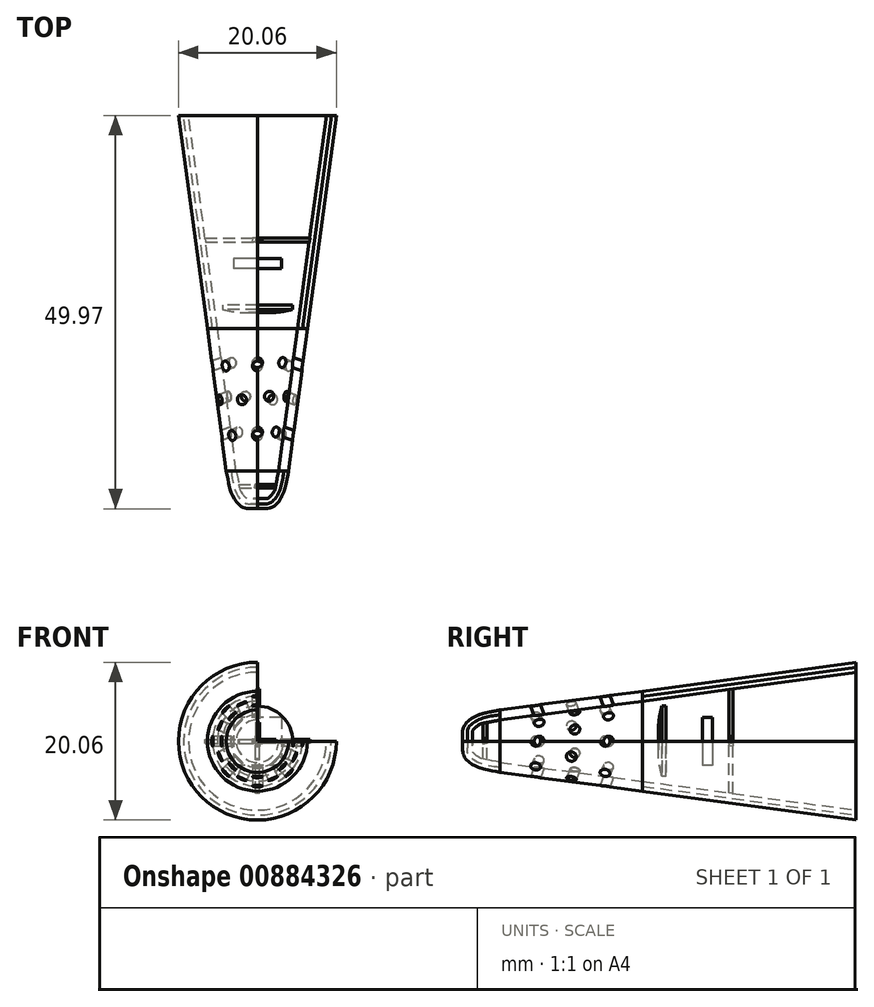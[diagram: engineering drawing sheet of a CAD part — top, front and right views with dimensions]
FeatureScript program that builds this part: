
annotation { "Feature Type Name" : "Feature", "Feature Type Description" : "" }
export const myFeature = defineFeature(function(context is Context, id is Id, definition is map)
    precondition{}
    {
        {
            var Q0;
            Q0=qCreatedBy(makeId("Right.planeOp"),FACE);
            var sketch = newSketch(context, id + "F0", { "sketchPlane" : qUnion([Q0])});
            skFitSpline(sketch, "E0", {"points": [v(0, 0) * mm, v(0, 1.1) * mm, v(0.45, 2.3) * mm, v(2.09, 3.34) * mm, v(4.76, 3.97) * mm], "startDerivative": vector(-0.16, 5.28) * mm, "endDerivative": vector(14.36, 3.06) * mm});
            skLineSegment(sketch, "E1", {"start": v(4.76, 3.97) * mm, "end": v(22.86, 6.35) * mm});
            skLineSegment(sketch, "E2", {"start": v(22.86, 6.35) * mm, "end": v(22.86, 0) * mm});
            skLineSegment(sketch, "E3", {"start": v(22.86, 0) * mm, "end": v(0, 0) * mm});
            skLineSegment(sketch, "E4", {"start": v(0, 0) * mm, "end": v(44.4, 0) * mm, "construction": true});
            skFitSpline(sketch, "E5", {"points": [v(1.27, 0) * mm, v(1.27, 1.1) * mm, v(1.34, 1.4) * mm, v(2.09, 2.07) * mm, v(4.76, 2.69) * mm], "startDerivative": vector(-0.16, 5.28) * mm, "endDerivative": vector(14.36, 3.06) * mm});
            skLineSegment(sketch, "E6", {"start": v(4.76, 2.69) * mm, "end": v(22.86, 5.08) * mm});
            skLineSegment(sketch, "E7", {"start": v(4.76, 3.97) * mm, "end": v(4.76, 2.69) * mm});
            skFitSpline(sketch, "E8", {"points": [v(0.62, 0) * mm, v(0.6, 1.05) * mm, v(0.7, 1.6) * mm, v(1.34, 2.32) * mm, v(2.5, 2.9) * mm, v(3.81, 3.22) * mm, v(4.76, 3.33) * mm], "startDerivative": vector(-0.15, 6.7) * mm, "endDerivative": vector(5.58, 0.48) * mm});
            skLineSegment(sketch, "E9", {"start": v(0.62, 0) * mm, "end": v(1.27, 0) * mm});
            skLineSegment(sketch, "E10", {"start": v(4.76, 3.33) * mm, "end": v(4.76, 2.69) * mm});
            skSolve(sketch);
        }
        {
            var Q0;
            {var subQ0=sQuery(id+"F0.wireOp",EDGE,"E0");Q0=makeQuery(id+"F0.imprint","IMPRINT",FACE,{"disambiguationData":[TD([[makeQuery(id+"F0.imprint","IMPRINT",EDGE,{"derivedFrom":subQ0}),-1.0]])]});}
            var Q1;
            Q1=sQuery(id+"F0.wireOp",EDGE,"E4");
            revolve(context, id + "F1", {"surfaceOperationType" : NewSurfaceOperationType.NEW, "entities" : qUnion([Q0]), "axis" : qUnion([Q1]), "revolveType" : RevolveType.FULL});
        }
        {
            var Q0;
            Q0=qCreatedBy(makeId("Right.planeOp"),FACE);
            var sketch = newSketch(context, id + "F2", { "sketchPlane" : qUnion([Q0])});
            skLineSegment(sketch, "E11", {"start": v(0, 0) * mm, "end": v(22.86, 0) * mm});
            skLineSegment(sketch, "E12", {"start": v(22.86, 0) * mm, "end": v(22.86, 6.35) * mm});
            skLineSegment(sketch, "E13", {"start": v(22.86, 6.35) * mm, "end": v(49.95, 10.03) * mm});
            skLineSegment(sketch, "E14", {"start": v(49.95, 10.03) * mm, "end": v(49.95, 0) * mm});
            skLineSegment(sketch, "E15", {"start": v(49.95, 0) * mm, "end": v(22.86, 0) * mm});
            skLineSegment(sketch, "E16", {"start": v(22.86, 6.35) * mm, "end": v(22.86, 5.08) * mm});
            skLineSegment(sketch, "E17", {"start": v(22.86, 5.08) * mm, "end": v(49.95, 8.76) * mm});
            skLineSegment(sketch, "E18", {"start": v(49.95, 8.76) * mm, "end": v(49.95, 10.03) * mm});
            skLineSegment(sketch, "E19", {"start": v(22.86, 5.71) * mm, "end": v(49.95, 9.4) * mm});
            skSolve(sketch);
        }
        {
            var Q0;
            {var subQ2=sQuery(id+"F2.wireOp",EDGE,"E13");Q0=makeQuery(id+"F2.imprint","IMPRINT",FACE,{"disambiguationData":[TD([[makeQuery(id+"F2.imprint","IMPRINT",EDGE,{"derivedFrom":subQ2}),-1.0]])]});}
            var Q1;
            Q1=sQuery(id+"F2.wireOp",EDGE,"E15");
            revolve(context, id + "F3", {"operationType" : NewBodyOperationType.ADD, "surfaceOperationType" : NewSurfaceOperationType.NEW, "entities" : qUnion([Q0]), "axis" : qUnion([Q1]), "revolveType" : RevolveType.FULL});
        }
        {
            var Q0;
            {var subQ4=sQuery(id+"F0.wireOp",EDGE,"E1");Q0=makeQuery(id+"F0.imprint","IMPRINT",FACE,{"disambiguationData":[TD([[makeQuery(id+"F0.imprint","IMPRINT",EDGE,{"derivedFrom":subQ4}),-1.0]])]});}
            var Q1;
            Q1=sQuery(id+"F0.wireOp",EDGE,"E3");
            revolve(context, id + "F4", {"surfaceOperationType" : NewSurfaceOperationType.NEW, "entities" : qUnion([Q0]), "axis" : qUnion([Q1]), "revolveType" : RevolveType.FULL});
        }
        {
            var Q0;
            {var subQ2=sQuery(id+"F2.wireOp",EDGE,"E17");Q0=makeQuery(id+"F2.imprint","IMPRINT",FACE,{"disambiguationData":[TD([[makeQuery(id+"F2.imprint","IMPRINT",EDGE,{"derivedFrom":subQ2}),1.0]])]});}
            var Q1;
            Q1=sQuery(id+"F2.wireOp",EDGE,"E15");
            revolve(context, id + "F5", {"surfaceOperationType" : NewSurfaceOperationType.NEW, "entities" : qUnion([Q0]), "axis" : qUnion([Q1]), "revolveType" : RevolveType.FULL});
        }
        {
            var Q0;
            {var subQ0=sQuery(id+"F0.wireOp",EDGE,"E5");Q0=makeQuery(id+"F0.imprint","IMPRINT",FACE,{"disambiguationData":[TD([[makeQuery(id+"F0.imprint","IMPRINT",EDGE,{"derivedFrom":subQ0}),1.0]])]});}
            var Q1;
            Q1=sQuery(id+"F2.wireOp",EDGE,"E11");
            revolve(context, id + "F6", {"surfaceOperationType" : NewSurfaceOperationType.NEW, "entities" : qUnion([Q0]), "axis" : qUnion([Q1]), "revolveType" : RevolveType.FULL});
        }
        {
            var Q0;
            Q0=sQuery(id+"F0.wireOp",EDGE,"E1");
            cPlane(context, id + "F7", {"entities" : qUnion([Q0]), "cplaneType" : CPlaneType.LINE_ANGLE, "offset" : 25.4 * mm, "angle" : 0 * degree, "width" : 152.4 * mm, "height" : 152.4 * mm});
        }
        {
            var Q0;
            Q0=qCreatedBy(id+"F7.planeOp",FACE);
            var sketch = newSketch(context, id + "F8", { "sketchPlane" : qUnion([Q0])});
            skCircle(sketch, "E20", {"center": v(0, 9.8) * mm, "radius": 0.64 * mm});
            skCircle(sketch, "E21", {"center": v(0, 18.7) * mm, "radius": 0.64 * mm});
            skLineSegment(sketch, "E22", {"start": v(0, 5.23) * mm, "end": v(0, 23.5) * mm});
            skSolve(sketch);
        }
        {
            var Q0;
            Q0=qCreatedBy(makeId("Right.planeOp"),FACE);
            var sketch = newSketch(context, id + "F9", { "sketchPlane" : qUnion([Q0])});
            skLineSegment(sketch, "E23", {"start": v(9.29, 4.57) * mm, "end": v(9.81, 3.13) * mm});
            skLineSegment(sketch, "E24", {"start": v(9.29, 4.57) * mm, "end": v(9.29, 0) * mm, "construction": true});
            skLineSegment(sketch, "E25", {"start": v(18.1, 5.72) * mm, "end": v(18.62, 4.3) * mm});
            skLineSegment(sketch, "E26", {"start": v(18.1, 5.72) * mm, "end": v(18.1, 0) * mm, "construction": true});
            skSolve(sketch);
        }
        {
            var Q0;
            {var subQ0=sQuery(id+"F8.wireOp",EDGE,"E22");var subQ1=sQuery(id+"F8.wireOp",EDGE,"E20");var subQ2=makeQuery(id+"F8.imprint","INTERSECT",VERTEX,{"disambiguationData":[OD(0.0)],"derivedFrom":[subQ1,subQ0]});Q0=makeQuery(id+"F8.imprint","IMPRINT",FACE,{"disambiguationData":[TD([[makeQuery(id+"F8.imprint","IMPRINT",EDGE,{"disambiguationData":[TD([[subQ2,1.0]])],"derivedFrom":subQ1}),1.0]])]});}
            var Q1;
            {var subQ0=sQuery(id+"F8.wireOp",EDGE,"E22");var subQ1=sQuery(id+"F8.wireOp",EDGE,"E20");var subQ2=makeQuery(id+"F8.imprint","INTERSECT",VERTEX,{"disambiguationData":[OD(0.0)],"derivedFrom":[subQ1,subQ0]});Q1=makeQuery(id+"F8.imprint","IMPRINT",FACE,{"disambiguationData":[TD([[makeQuery(id+"F8.imprint","IMPRINT",EDGE,{"disambiguationData":[TD([[subQ2,-1.0]])],"derivedFrom":subQ1}),1.0]])]});}
            var Q2;
            Q2=sQuery(id+"F9.wireOp",EDGE,"E23");
            sweep(context, id + "F10", {"profiles" : qUnion([Q0, Q1]), "path" : qUnion([Q2])});
        }
        {
            var Q0;
            {var subQ0=sQuery(id+"F8.wireOp",EDGE,"E22");var subQ1=sQuery(id+"F8.wireOp",EDGE,"E21");var subQ2=makeQuery(id+"F8.imprint","INTERSECT",VERTEX,{"disambiguationData":[OD(0.0)],"derivedFrom":[subQ1,subQ0]});Q0=makeQuery(id+"F8.imprint","IMPRINT",FACE,{"disambiguationData":[TD([[makeQuery(id+"F8.imprint","IMPRINT",EDGE,{"disambiguationData":[TD([[subQ2,1.0]])],"derivedFrom":subQ1}),1.0]])]});}
            var Q1;
            {var subQ0=sQuery(id+"F8.wireOp",EDGE,"E22");var subQ1=sQuery(id+"F8.wireOp",EDGE,"E21");var subQ2=makeQuery(id+"F8.imprint","INTERSECT",VERTEX,{"disambiguationData":[OD(0.0)],"derivedFrom":[subQ1,subQ0]});Q1=makeQuery(id+"F8.imprint","IMPRINT",FACE,{"disambiguationData":[TD([[makeQuery(id+"F8.imprint","IMPRINT",EDGE,{"disambiguationData":[TD([[subQ2,-1.0]])],"derivedFrom":subQ1}),1.0]])]});}
            var Q2;
            Q2=sQuery(id+"F9.wireOp",EDGE,"E25");
            sweep(context, id + "F11", {"profiles" : qUnion([Q0, Q1]), "path" : qUnion([Q2])});
        }
        {
            var Q0;
            Q0=makeQuery(id+"F10.opSweep","SWEPT_BODY",BODY,{"disambiguationData":[OSD([sQuery(id+"F8.wireOp",EDGE,"E20"),sQuery(id+"F9.wireOp",EDGE,"E23")])]});
            var Q1;
            Q1=makeQuery(id+"F11.opSweep","SWEPT_BODY",BODY,{"disambiguationData":[OSD([sQuery(id+"F8.wireOp",EDGE,"E21"),sQuery(id+"F9.wireOp",EDGE,"E25")])]});
            var Q2;
            Q2=makeQuery(id+"F4.opRevolve","SWEPT_EDGE",EDGE,{"disambiguationData":[OSD([sQuery(id+"F0.wireOp",EDGE,"E1"),sQuery(id+"F0.wireOp",EDGE,"E2")])]});
            var Q3;
            Q3=makeQuery(id+"F4.opRevolve","SWEPT_BODY",BODY,{"disambiguationData":[OSD([sQuery(id+"F0.wireOp",EDGE,"E1"),sQuery(id+"F0.wireOp",EDGE,"E2"),sQuery(id+"F0.wireOp",EDGE,"E6"),sQuery(id+"F0.wireOp",EDGE,"E7")])]});
            circularPattern(context, id + "F12", {"operationType" : NewBodyOperationType.REMOVE, "entities" : qUnion([Q0, Q1]), "axis" : qUnion([Q2]), "angle" : 360 * degree, "instanceCount" : 8, "equalSpace" : true, "isCentered" : true});
        }
        {
            var Q0;
            Q0=sQuery(id+"F0.wireOp",EDGE,"E4");
            cPlane(context, id + "F13", {"entities" : qUnion([Q0]), "cplaneType" : CPlaneType.LINE_ANGLE, "offset" : 25.4 * mm, "angle" : 22.5 * degree, "width" : 152.4 * mm, "height" : 152.4 * mm});
        }
        {
            var Q0;
            Q0=qCreatedBy(id+"F13.planeOp",FACE);
            var sketch = newSketch(context, id + "F14", { "sketchPlane" : qUnion([Q0])});
            skLineSegment(sketch, "E27", {"start": v(-6.35, 22.86) * mm, "end": v(-3.97, 4.76) * mm});
            skLineSegment(sketch, "E28", {"start": v(3.97, 4.76) * mm, "end": v(6.35, 22.86) * mm});
            skSolve(sketch);
        }
        {
            var Q0;
            Q0=sQuery(id+"F14.wireOp",EDGE,"E27");
            cPlane(context, id + "F15", {"entities" : qUnion([Q0]), "cplaneType" : CPlaneType.LINE_ANGLE, "offset" : 25.4 * mm, "angle" : 67.5 * degree, "width" : 152.4 * mm, "height" : 152.4 * mm});
        }
        {
            var Q0;
            Q0=qCreatedBy(id+"F15.planeOp",FACE);
            var sketch = newSketch(context, id + "F16", { "sketchPlane" : qUnion([Q0])});
            skLineSegment(sketch, "E29", {"start": v(23.5, 0.02) * mm, "end": v(5.23, 0.01) * mm, "construction": true});
            skCircle(sketch, "E30", {"center": v(14.38, 0.02) * mm, "radius": 0.64 * mm});
            skSolve(sketch);
        }
        {
            var Q0;
            Q0=qCreatedBy(id+"F13.planeOp",FACE);
            var sketch = newSketch(context, id + "F17", { "sketchPlane" : qUnion([Q0])});
            skLineSegment(sketch, "E31", {"start": v(-5.16, 13.82) * mm, "end": v(-3.73, 14.34) * mm});
            skLineSegment(sketch, "E32", {"start": v(-5.16, 13.82) * mm, "end": v(0, 13.82) * mm});
            skLineSegment(sketch, "E33", {"start": v(-3.73, 14.34) * mm, "end": v(-6.51, 13.33) * mm});
            skSolve(sketch);
        }
        {
            var Q0;
            Q0=makeQuery(id+"F16.imprint","IMPRINT",FACE,{"disambiguationData":[TD([[makeQuery(id+"F16.imprint","IMPRINT",EDGE,{"derivedFrom":sQuery(id+"F16.wireOp",EDGE,"E30")}),1.0]])]});
            var Q1;
            Q1=sQuery(id+"F17.wireOp",EDGE,"E33");
            sweep(context, id + "F18", {"profiles" : qUnion([Q0]), "path" : qUnion([Q1])});
        }
        {
            var Q0;
            Q0=makeQuery(id+"F18.opSweep","SWEPT_BODY",BODY,{"disambiguationData":[OSD([sQuery(id+"F16.wireOp",EDGE,"E30"),sQuery(id+"F17.wireOp",EDGE,"E31")])]});
            var Q1;
            Q1=makeQuery(id+"F3.opRevolve","SWEPT_EDGE",EDGE,{"disambiguationData":[OSD([sQuery(id+"F2.wireOp",EDGE,"E12"),sQuery(id+"F2.wireOp",EDGE,"E13")])]});
            circularPattern(context, id + "F19", {"operationType" : NewBodyOperationType.REMOVE, "entities" : qUnion([Q0]), "axis" : qUnion([Q1]), "angle" : 360 * degree, "instanceCount" : 8, "equalSpace" : true});
        }
        {
            var Q0;
            Q0=qCreatedBy(makeId("Right.planeOp"),FACE);
            var sketch = newSketch(context, id + "F20", { "sketchPlane" : qUnion([Q0])});
            skLineSegment(sketch, "E34.bottom", {"start": v(-2.98, 0) * mm, "end": v(62.48, 0) * mm});
            skLineSegment(sketch, "E34.top", {"start": v(-2.98, 18.36) * mm, "end": v(62.48, 18.36) * mm});
            skLineSegment(sketch, "E34.left", {"start": v(-2.98, 0) * mm, "end": v(-2.98, 18.36) * mm});
            skLineSegment(sketch, "E34.right", {"start": v(62.48, 0) * mm, "end": v(62.48, 18.36) * mm});
            skSolve(sketch);
        }
        {
            var Q0;
            Q0=makeQuery(id+"F20.imprint","IMPRINT",FACE,{"disambiguationData":[TD([[makeQuery(id+"F20.imprint","IMPRINT",EDGE,{"derivedFrom":sQuery(id+"F20.wireOp",EDGE,"E34.bottom")}),1.0]])]});
            extrude(context, id + "F21", {"entities" : qUnion([Q0]), "operationType" : NewBodyOperationType.REMOVE, "depth" : 25.4 * mm, "offsetDistance" : 25.4 * mm});
        }
        {
            var Q0;
            Q0=qCreatedBy(makeId("Right.planeOp"),FACE);
            var sketch = newSketch(context, id + "F22", { "sketchPlane" : qUnion([Q0])});
            skLineSegment(sketch, "E35", {"start": v(25.85, 0) * mm, "end": v(25.85, 4.46) * mm});
            skLineSegment(sketch, "E36", {"start": v(25.85, 4.46) * mm, "end": v(25.3, 4.46) * mm});
            skFitSpline(sketch, "E37", {"points": [v(25.3, 4.46) * mm, v(24.93, 2.4) * mm, v(24.88, 0.71) * mm, v(24.9, 0.36) * mm, v(24.9, 0) * mm], "startDerivative": vector(-1.24, -5.47) * mm, "endDerivative": vector(0.04, -2.48) * mm});
            skLineSegment(sketch, "E38", {"start": v(24.9, 0) * mm, "end": v(25.85, 0) * mm});
            skSolve(sketch);
        }
        {
            var Q0;
            Q0=makeQuery(id+"F22.imprint","IMPRINT",FACE,{"disambiguationData":[TD([[makeQuery(id+"F22.imprint","IMPRINT",EDGE,{"derivedFrom":sQuery(id+"F22.wireOp",EDGE,"E35")}),1.0]])]});
            var Q1;
            Q1=sQuery(id+"F22.wireOp",EDGE,"E38");
            revolve(context, id + "F23", {"surfaceOperationType" : NewSurfaceOperationType.NEW, "entities" : qUnion([Q0]), "axis" : qUnion([Q1]), "revolveType" : RevolveType.FULL});
        }
        {
            var Q0;
            Q0=qCreatedBy(makeId("Front.planeOp"),FACE);
            cPlane(context, id + "F24", {"entities" : qUnion([Q0]), "cplaneType" : CPlaneType.OFFSET, "offset" : 30.48 * mm, "oppositeDirection" : true, "width" : 152.4 * mm, "height" : 152.4 * mm});
        }
        {
            var Q0;
            Q0=qCreatedBy(id+"F24.planeOp",FACE);
            var sketch = newSketch(context, id + "F25", { "sketchPlane" : qUnion([Q0])});
            skLineSegment(sketch, "E39.bottom", {"start": v(3.05, 3.05) * mm, "end": v(-3.05, 3.05) * mm});
            skLineSegment(sketch, "E39.top", {"start": v(3.05, -3.05) * mm, "end": v(-3.05, -3.05) * mm});
            skLineSegment(sketch, "E39.left", {"start": v(3.05, 3.05) * mm, "end": v(3.05, -3.05) * mm});
            skLineSegment(sketch, "E39.right", {"start": v(-3.05, 3.05) * mm, "end": v(-3.05, -3.05) * mm});
            skSolve(sketch);
        }
        {
            var Q0;
            Q0=makeQuery(id+"F25.imprint","IMPRINT",FACE,{"disambiguationData":[TD([[makeQuery(id+"F25.imprint","IMPRINT",EDGE,{"derivedFrom":sQuery(id+"F25.wireOp",EDGE,"E39.bottom")}),1.0]])]});
            extrude(context, id + "F26", {"entities" : qUnion([Q0]), "oppositeDirection" : true, "depth" : 1.27 * mm, "offsetDistance" : 25.4 * mm});
        }
        {
            var Q0;
            Q0=qCreatedBy(makeId("Right.planeOp"),FACE);
            var sketch = newSketch(context, id + "F27", { "sketchPlane" : qUnion([Q0])});
            skLineSegment(sketch, "E40", {"start": v(2.62, 2.28) * mm, "end": v(4.76, 2.69) * mm});
            skSolve(sketch);
        }
        {
            var Q0;
            Q0=sQuery(id+"F27.wireOp",EDGE,"E40");
            cPlane(context, id + "F28", {"entities" : qUnion([Q0]), "cplaneType" : CPlaneType.LINE_ANGLE, "offset" : 25.4 * mm, "angle" : 0 * degree, "width" : 152.4 * mm, "height" : 152.4 * mm});
        }
        {
            var Q0;
            Q0=qCreatedBy(id+"F28.planeOp",FACE);
            var sketch = newSketch(context, id + "F29", { "sketchPlane" : qUnion([Q0])});
            skLineSegment(sketch, "E41.bottom", {"start": v(-0.25, 3.48) * mm, "end": v(0.25, 3.48) * mm});
            skLineSegment(sketch, "E41.top", {"start": v(-0.25, 2.97) * mm, "end": v(0.25, 2.97) * mm});
            skLineSegment(sketch, "E41.left", {"start": v(-0.25, 3.48) * mm, "end": v(-0.25, 2.97) * mm});
            skLineSegment(sketch, "E41.right", {"start": v(0.25, 3.48) * mm, "end": v(0.25, 2.97) * mm});
            skLineSegment(sketch, "E42", {"start": v(0, 2.97) * mm, "end": v(0, 3.48) * mm, "construction": true});
            skLineSegment(sketch, "E43", {"start": v(-0.25, 3.23) * mm, "end": v(0.25, 3.23) * mm, "construction": true});
            skSolve(sketch);
        }
        {
            var Q0;
            Q0=qCreatedBy(makeId("Right.planeOp"),FACE);
            var sketch = newSketch(context, id + "F30", { "sketchPlane" : qUnion([Q0])});
            skLineSegment(sketch, "E44", {"start": v(2.84, 2.32) * mm, "end": v(2.84, -0.36) * mm});
            skSolve(sketch);
        }
        {
            var Q0;
            Q0=makeQuery(id+"F29.imprint","IMPRINT",FACE,{"disambiguationData":[TD([[makeQuery(id+"F29.imprint","IMPRINT",EDGE,{"derivedFrom":sQuery(id+"F29.wireOp",EDGE,"E41.bottom")}),-1.0]])]});
            var Q1;
            Q1=sQuery(id+"F30.wireOp",EDGE,"E44");
            sweep(context, id + "F31", {"profiles" : qUnion([Q0]), "path" : qUnion([Q1])});
        }
        {
            var Q0;
            Q0=makeQuery(id+"F31.opSweep","SWEPT_BODY",BODY,{"disambiguationData":[OSD([sQuery(id+"F29.wireOp",EDGE,"E41.bottom"),sQuery(id+"F29.wireOp",EDGE,"E41.top"),sQuery(id+"F29.wireOp",EDGE,"E41.left"),sQuery(id+"F29.wireOp",EDGE,"E41.right"),sQuery(id+"F30.wireOp",EDGE,"E44")])]});
            var Q1;
            Q1=sQuery(id+"F0.wireOp",EDGE,"E3");
            circularPattern(context, id + "F32", {"entities" : qUnion([Q0]), "axis" : qUnion([Q1]), "angle" : 360 * degree, "instanceCount" : 4, "equalSpace" : true});
        }
        {
            var Q0;
            Q0=makeQuery(id+"F21.boolean.opBoolean","INTERSECT",EDGE,{"derivedFrom":[makeQuery(id+"F5.opRevolve","SWEPT_FACE",FACE,{"disambiguationData":[OSD([sQuery(id+"F2.wireOp",EDGE,"E17")])]}),makeQuery(id+"F21.opExtrude","CAP_FACE",FACE,{"disambiguationData":[OSD([sQuery(id+"F20.wireOp",EDGE,"E34.bottom"),sQuery(id+"F20.wireOp",EDGE,"E34.top"),sQuery(id+"F20.wireOp",EDGE,"E34.left"),sQuery(id+"F20.wireOp",EDGE,"E34.right")])],"isStart":true})]});
            cPlane(context, id + "F33", {"entities" : qUnion([Q0]), "cplaneType" : CPlaneType.LINE_ANGLE, "offset" : 25.4 * mm, "angle" : 0 * degree, "width" : 152.4 * mm, "height" : 152.4 * mm});
        }
        {
            var Q0;
            Q0=qCreatedBy(id+"F33.planeOp",FACE);
            var sketch = newSketch(context, id + "F34", { "sketchPlane" : qUnion([Q0])});
            skLineSegment(sketch, "E45.bottom", {"start": v(-0.25, -34.95) * mm, "end": v(0.25, -34.95) * mm});
            skLineSegment(sketch, "E45.top", {"start": v(-0.25, -34.44) * mm, "end": v(0.25, -34.44) * mm});
            skLineSegment(sketch, "E45.left", {"start": v(-0.25, -34.95) * mm, "end": v(-0.25, -34.44) * mm});
            skLineSegment(sketch, "E45.right", {"start": v(0.25, -34.95) * mm, "end": v(0.25, -34.44) * mm});
            skLineSegment(sketch, "E46", {"start": v(0, -34.44) * mm, "end": v(0, -34.95) * mm, "construction": true});
            skLineSegment(sketch, "E47", {"start": v(-0.25, -34.7) * mm, "end": v(0.25, -34.7) * mm, "construction": true});
            skSolve(sketch);
        }
        {
            var Q0;
            Q0=qCreatedBy(makeId("Right.planeOp"),FACE);
            var sketch = newSketch(context, id + "F35", { "sketchPlane" : qUnion([Q0])});
            skLineSegment(sketch, "E48", {"start": v(34.12, 6.63) * mm, "end": v(34.12, -0.62) * mm});
            skSolve(sketch);
        }
        {
            var Q0;
            Q0=makeQuery(id+"F34.imprint","IMPRINT",FACE,{"disambiguationData":[TD([[makeQuery(id+"F34.imprint","IMPRINT",EDGE,{"derivedFrom":sQuery(id+"F34.wireOp",EDGE,"E45.bottom")}),1.0]])]});
            var Q1;
            Q1=sQuery(id+"F35.wireOp",EDGE,"E48");
            sweep(context, id + "F36", {"profiles" : qUnion([Q0]), "path" : qUnion([Q1])});
        }
        {
            var Q0;
            Q0=makeQuery(id+"F36.opSweep","SWEPT_BODY",BODY,{"disambiguationData":[OSD([sQuery(id+"F34.wireOp",EDGE,"E45.bottom"),sQuery(id+"F34.wireOp",EDGE,"E45.top"),sQuery(id+"F34.wireOp",EDGE,"E45.left"),sQuery(id+"F34.wireOp",EDGE,"E45.right"),sQuery(id+"F35.wireOp",EDGE,"E48")])]});
            var Q1;
            Q1=sQuery(id+"F0.wireOp",EDGE,"E4");
            circularPattern(context, id + "F37", {"entities" : qUnion([Q0]), "axis" : qUnion([Q1]), "angle" : 360 * degree, "instanceCount" : 4, "equalSpace" : true});
        }
    });
